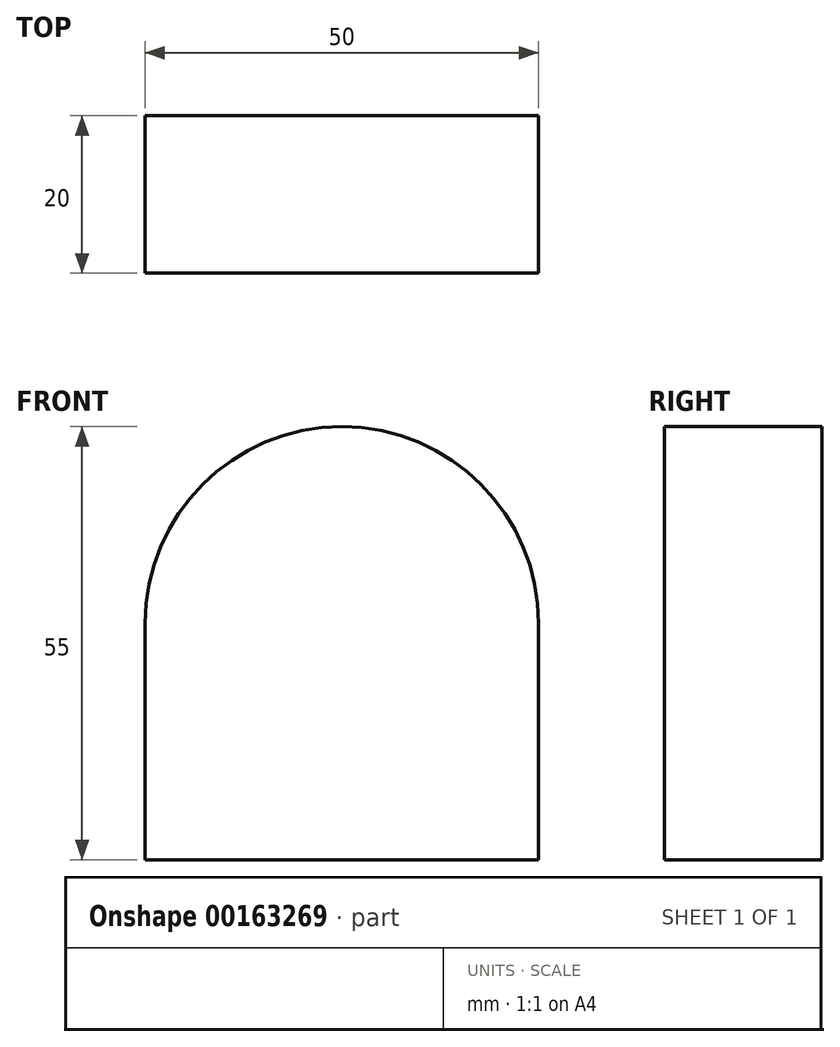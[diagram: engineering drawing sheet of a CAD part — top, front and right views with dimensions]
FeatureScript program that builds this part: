
annotation { "Feature Type Name" : "Feature", "Feature Type Description" : "" }
export const myFeature = defineFeature(function(context is Context, id is Id, definition is map)
    precondition{}
    {
        {
            var Q0;
            Q0=qCreatedBy(makeId("Front.planeOp"),FACE);
            var sketch = newSketch(context, id + "F0", { "sketchPlane" : qUnion([Q0])});
            skLineSegment(sketch, "E0.bottom", {"start": v(-25, -15) * mm, "end": v(25, -15) * mm});
            skLineSegment(sketch, "E0.top", {"start": v(-25, 15) * mm, "end": v(25, 15) * mm, "construction": true});
            skLineSegment(sketch, "E0.left", {"start": v(-25, -15) * mm, "end": v(-25, 15) * mm});
            skLineSegment(sketch, "E0.right", {"start": v(25, -15) * mm, "end": v(25, 15) * mm});
            skPoint(sketch, "E0.middle", {"position": v(0, 0) * mm});
            skArc(sketch, "E1", {"start": v(25, 15) * mm, "mid": v(0, 40) * mm, "end": v(-25, 15) * mm});
            skSolve(sketch);
        }
        {
            var Q0;
            Q0 = qSketchRegion(id + "F0", true);
            extrude(context, id + "F1", {"entities" : qUnion([Q0]), "depth" : 20 * mm});
        }
    });
